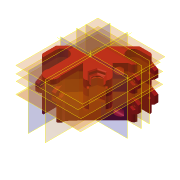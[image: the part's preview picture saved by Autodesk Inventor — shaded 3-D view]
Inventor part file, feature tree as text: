
AUTODESK INVENTOR PART (.ipt)
format: ipt  version: 2015 SP2 (Build 190223200, 223)  size: 684,544 bytes
history: native  units: mm
features: extrude x24, sketch x23, projected_geometry x15, plane x7, chamfer x4, mirror x2, fillet x2, other x1, reference x1
ambient origin geometry x8: Origin, YZ Plane, XZ Plane, XY Plane, X Axis, Y Axis, Z Axis, Center Point
bodies: Body1 (feature_tree)
feature tree (79):
  other  "Sólido1"
  extrude  "Extrusión1"  Depth=16.0mm
  extrude  "Extrusión2"  Depth=4.0mm
  extrude  "Extrusión3"  Depth=4.62mm
  extrude  "Extrusión4"  Depth=11.7mm
  plane  "Plano de trabajo1"
  extrude  "Extrusión8"  Depth=24.0mm
  extrude  "Extrusión9"  TaperAngle=120.0deg  [1 undecoded]
  extrude  "Extrusión10"  Depth=25.0mm
  extrude  "Extrusión11"  Depth=21.0mm
  extrude  "Extrusión12"  Depth=4.0mm
  extrude  "Extrusión13"  Depth=5.0mm TaperAngle=0.0deg
  extrude  "Extrusión14"  Depth=2.0mm
  plane  "Plano de trabajo2"
  mirror  "Simetría1"
  extrude  "Extrusión15"  Depth=25.0mm TaperAngle=0.0deg
  extrude  "Extrusión16"  Depth=44.0mm
  extrude  "Extrusión17"  Depth=10.0mm TaperAngle=0.0deg
  plane  "Plano de trabajo3"
  mirror  "Simetría2"
  plane  "Plano de trabajo4"
  extrude  "Extrusión18"  Depth=10.0mm TaperAngle=0.0deg
  extrude  "Extrusión19"  Depth=5.5mm TaperAngle=0.0deg
  plane  "Plano de trabajo5"
  extrude  "Extrusión20"  Depth=3.5mm TaperAngle=0.0deg
  extrude  "Extrusión21"  Depth=8.3mm
  extrude  "Extrusión22"  Depth=7.75mm
  plane  "Plano de trabajo6"
  plane  "Plano de trabajo7"
  extrude  "Extrusión27"  Depth=25.0mm TaperAngle=0.0deg
  extrude  "Extrusión28"  Depth=6.0mm
  fillet  "Empalme1"  Radius=26.0mm
  chamfer  "Chaflán1"  Distance=2.0mm
  chamfer  "Chaflán2"  Distance=30.0mm
  chamfer  "Chaflán3"  Distance=6.235mm
  extrude  "Extrusión29"  Depth=1.0mm TaperAngle=0.0deg
  extrude  "Extrusión30"  Depth=1.0mm TaperAngle=0.0deg
  extrude  "Extrusion31"  Depth=1.0mm
  chamfer  "Chamfer4"  Distance=14.0mm
  fillet  "Empalme2"  Radius=15.75mm
  sketch  "Boceto1"  dims[d0=20.0mm d3=16.0mm]
  sketch  "Boceto2"  dims[d7=4.0mm d8=4.0mm]
  projected_geometry  "Contorno proyectado1"
  sketch  "Boceto3"  dims[d10=5.56mm d11=4.62mm]
  projected_geometry  "Contorno proyectado2"
  sketch  "Boceto4"  dims[d12=13.1mm d13=11.7mm]
  projected_geometry  "Contorno proyectado3"
  sketch  "Boceto7"  dims[d14=11.7mm d15=24.0mm]
  projected_geometry  "Contorno proyectado5"
  sketch  "Boceto8"  dims[d16=24.0mm d17=120.0deg]
  sketch  "Boceto9"  dims[d18=0.0mm d19=25.0mm]
  sketch  "Boceto10"  dims[d21=7.5mm d23=21.0mm]
  projected_geometry  "Contorno proyectado6"
  sketch  "Boceto11"  dims[d24=18.0mm d25=4.0mm]
  projected_geometry  "Contorno proyectado7"
  sketch  "Boceto12"  dims[d26=14.3mm d28=5.0mm d29=0.0mm]
  projected_geometry  "Contorno proyectado8"
  sketch  "Boceto13"  dims[d30=4.0mm d31=2.0mm]
  projected_geometry  "Contorno proyectado9"
  sketch  "Boceto14"  dims[d32=25.5mm d33=0.0mm d34=25.0mm d35=0.0mm]
  projected_geometry  "Contorno proyectado10"
  sketch  "Boceto15"  dims[d36=25.0mm d37=44.0mm]
  sketch  "Boceto16"  dims[d38=10.0mm d39=10.0mm d40=0.0mm]
  projected_geometry  "Contorno proyectado11"
  sketch  "Boceto17"  dims[d47=-27.75mm d48=10.0mm d49=0.0mm]
  projected_geometry  "Contorno proyectado12"
  sketch  "Boceto18"  dims[d50=13.4mm d51=5.5mm d52=0.0mm]
  projected_geometry  "Contorno proyectado13"
  projected_geometry  "Contorno proyectado14"
  sketch  "Boceto19"  dims[d53=9.0mm d54=3.5mm d55=0.0mm]
  sketch  "Boceto20"  dims[d56=8.3mm d57=8.3mm]
  sketch  "Boceto21"  dims[d58=40.0mm d59=7.75mm]
  reference  "Referencia1"
  sketch  "Boceto27"  dims[d60=11.0mm d61=25.0mm d62=0.0mm]
  projected_geometry  "Contorno proyectado15"
  sketch  "Boceto28"  dims[d63=3.0mm d64=6.0mm d65=26.0mm d66=0.0mm]
  projected_geometry  "Contorno proyectado16"
  sketch  "Boceto29"  dims[d67=7.0mm d68=2.0mm d69=0.0mm]
  sketch  "Sketch30"  dims[d70=3.75mm d71=30.0mm d72=0.0mm d73=6.235mm d74=3.0mm d75=0.0mm d76=3.0mm d77=0.0mm d78=24.0mm d79=14.0mm d80=15.75mm d81=2.0mm d82=3.0mm d83=0.0mm d84=7.0mm d85=7.0mm d86=2.0mm d87=0.0mm d88=3.75mm d89=3.75mm d90=30.0mm d91=0.0mm d92=6.235mm d93=6.235mm d94=2.8mm d95=0.0mm d97=56.215mm d98=7.15mm d99=23.562459mm d100=23.564405mm d101=11.748517mm d102=2.076246mm d103=15.1mm d104=24.2mm d105=0.0mm d106=15.1mm d107=48.4mm d108=0.0mm d109=6.486408mm d110=6.551017mm d111=6.548983mm d112=120.0deg d113=120.0deg d114=0.425mm d115=20.5mm d116=19.841009mm d118=14.3mm d127=-8.0mm d128=16.4mm d129=10.0mm d130=2.2mm d131=0.0mm d132=5.0mm d133=1.5mm d134=0.0mm d135=0.5mm d136=1.0mm d137=2.0mm d138=45.0deg d139=1.5mm d140=2.0mm d141=30.0deg d142=1.5mm d143=2.0mm d144=30.0deg d145=2.0mm d146=120.0deg d147=10.0mm d148=0.0mm d149=2.0mm d152=120.0deg d153=10.0mm d154=0.0mm d155=9.0mm d156=10.0mm d157=0.0mm d158=1.0mm d159=2.0mm d160=45.0deg d161=1.0mm]
note: 1 required parameter value undecoded (feature->parameter linkage not recoverable at this tier; creation-order binding heuristic only, values carry confidence <= 0.55)
